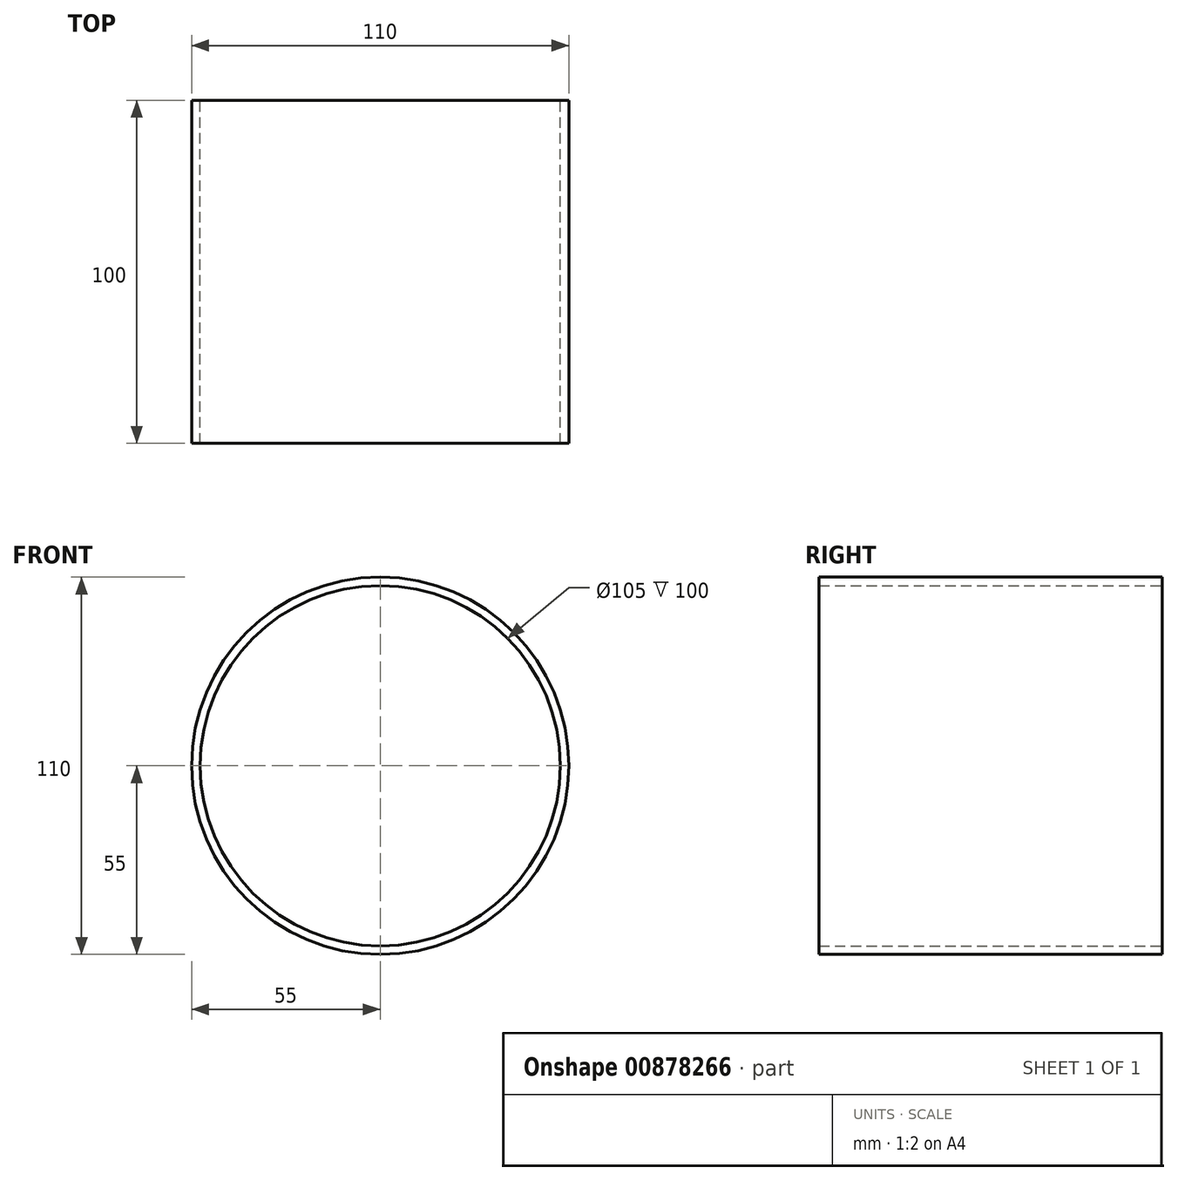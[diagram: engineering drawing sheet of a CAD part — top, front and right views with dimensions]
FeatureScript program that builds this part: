
annotation { "Feature Type Name" : "Feature", "Feature Type Description" : "" }
export const myFeature = defineFeature(function(context is Context, id is Id, definition is map)
    precondition{}
    {
        {
            var Q0;
            Q0=qCreatedBy(makeId("Front.planeOp"),FACE);
            var sketch = newSketch(context, id + "F0", { "sketchPlane" : qUnion([Q0])});
            skCircle(sketch, "E0", {"center": v(0, 0) * mm, "radius": 52.5 * mm});
            skCircle(sketch, "E1", {"center": v(0, 0) * mm, "radius": 55 * mm});
            skSolve(sketch);
        }
        {
            var Q0;
            Q0=makeQuery(id+"F0.imprint","IMPRINT",FACE,{"disambiguationData":[TD([[makeQuery(id+"F0.imprint","IMPRINT",EDGE,{"derivedFrom":sQuery(id+"F0.wireOp",EDGE,"E0")}),-1.0]])]});
            extrude(context, id + "F1", {"entities" : qUnion([Q0]), "depth" : 100 * mm, "offsetDistance" : 25 * mm});
        }
    });
